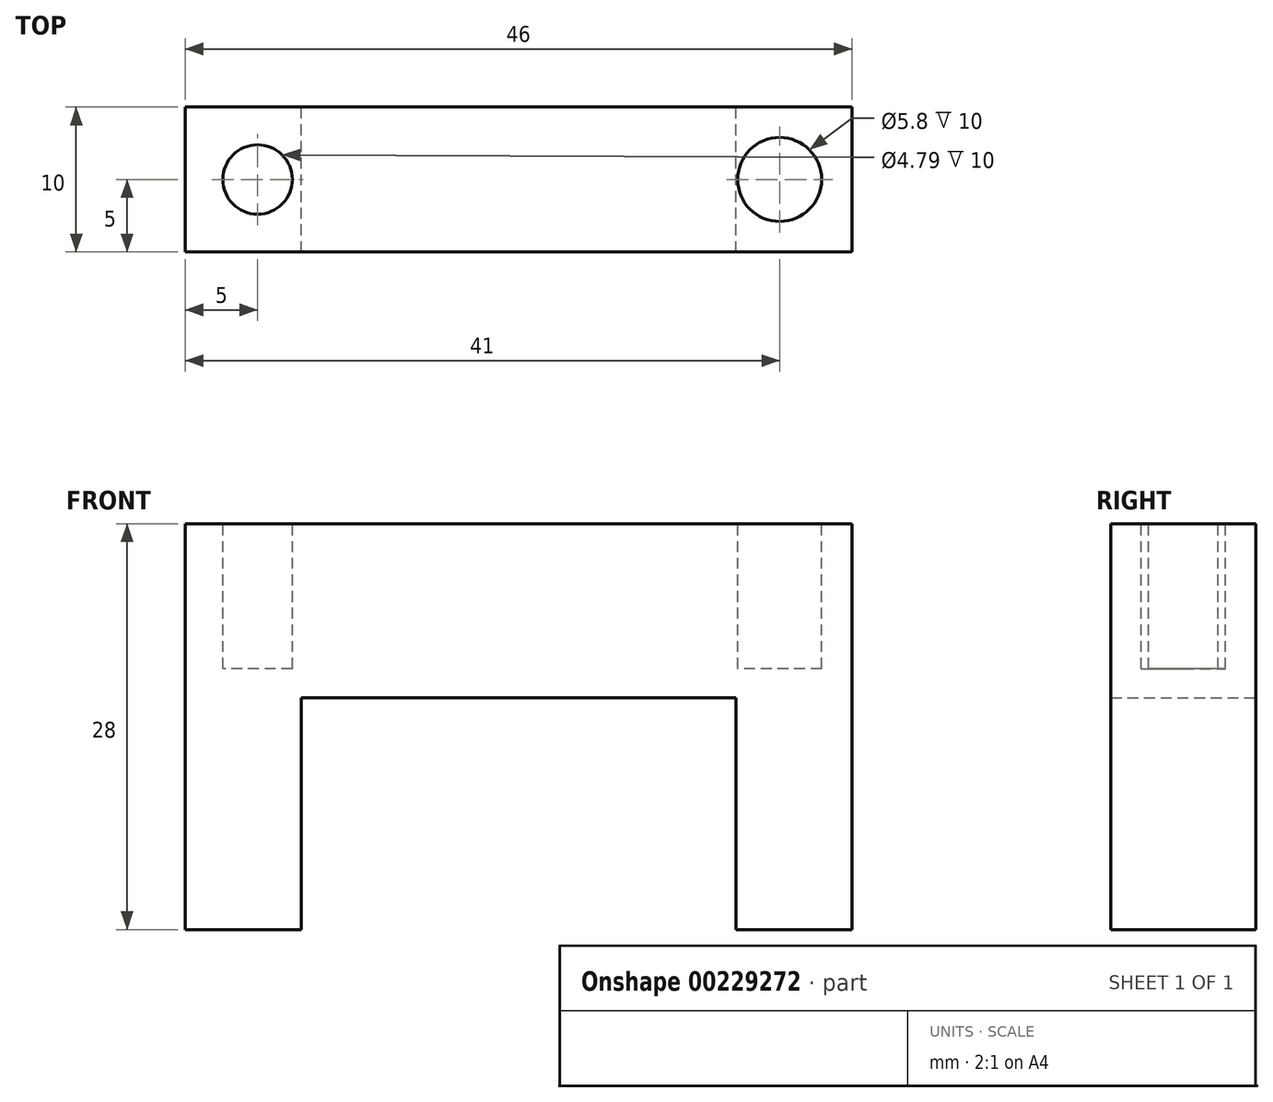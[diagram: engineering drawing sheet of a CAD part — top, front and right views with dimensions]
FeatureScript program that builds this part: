
annotation { "Feature Type Name" : "Feature", "Feature Type Description" : "" }
export const myFeature = defineFeature(function(context is Context, id is Id, definition is map)
    precondition{}
    {
        {
            var Q0;
            Q0=qCreatedBy(makeId("Front.planeOp"),FACE);
            var sketch = newSketch(context, id + "F0", { "sketchPlane" : qUnion([Q0])});
            skLineSegment(sketch, "E0.bottom", {"start": v(-23, 6) * mm, "end": v(23, 6) * mm});
            skLineSegment(sketch, "E0.top", {"start": v(-23, -6) * mm, "end": v(23, -6) * mm});
            skLineSegment(sketch, "E0.left", {"start": v(-23, 6) * mm, "end": v(-23, -6) * mm});
            skLineSegment(sketch, "E0.right", {"start": v(23, 6) * mm, "end": v(23, -6) * mm});
            skPoint(sketch, "E0.middle", {"position": v(0, 0) * mm});
            skLineSegment(sketch, "E1", {"start": v(-23, -6) * mm, "end": v(-23, -22) * mm});
            skLineSegment(sketch, "E2", {"start": v(-23, -22) * mm, "end": v(-15, -22) * mm});
            skLineSegment(sketch, "E3", {"start": v(-15, -22) * mm, "end": v(-15, -6) * mm});
            skLineSegment(sketch, "E4", {"start": v(23, -6) * mm, "end": v(23, -22) * mm});
            skLineSegment(sketch, "E5", {"start": v(23, -22) * mm, "end": v(15, -22) * mm});
            skLineSegment(sketch, "E6", {"start": v(15, -22) * mm, "end": v(15, -6) * mm});
            skSolve(sketch);
        }
        {
            var Q0;
            Q0 = qSketchRegion(id + "F0", true);
            extrude(context, id + "F1", {"entities" : qUnion([Q0]), "depth" : 10 * mm});
        }
        {
            var Q0;
            Q0=makeQuery(id+"F1.opExtrude","SWEPT_FACE",FACE,{"disambiguationData":[OSD([sQuery(id+"F0.wireOp",EDGE,"E0.bottom")])]});
            var sketch = newSketch(context, id + "F2", { "sketchPlane" : qUnion([Q0])});
            skCircle(sketch, "E7", {"center": v(-18, -5) * mm, "radius": 2.4 * mm});
            skCircle(sketch, "E8", {"center": v(18, -5) * mm, "radius": 2.9 * mm});
            skSolve(sketch);
        }
        {
            var Q0;
            Q0 = qSketchRegion(id + "F2", true);
            extrude(context, id + "F3", {"entities" : qUnion([Q0]), "operationType" : NewBodyOperationType.REMOVE, "oppositeDirection" : true, "depth" : 10 * mm});
        }
    });
